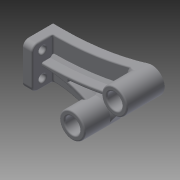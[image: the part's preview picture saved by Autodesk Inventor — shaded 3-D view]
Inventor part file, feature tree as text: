
AUTODESK INVENTOR PART (.ipt)
format: ipt  version: 2014 (Build 180170000, 170)  size: 399,360 bytes
history: native  units: in
note: dims shown in document units (in); Inventor stores cm internally (conversion verified against a paired STEP export)
features: extrude x6, sketch x6, fillet x2, chamfer x1
ambient origin geometry x8: Origin, YZ Plane, XZ Plane, XY Plane, X Axis, Y Axis, Z Axis, Center Point
bodies: Solid1 (feature_tree)
feature tree (15):
  extrude  "Extrusion1"  Depth=1.1713in
  extrude  "Extrusion2"  Depth=5.9055in
  extrude  "Extrusion3"  Depth=0.5315in
  extrude  "Extrusion4"  Depth=1.0441in
  extrude  "Extrusion5"  Depth=1.1024in
  chamfer  "Chamfer1"  Distance=0.8661in
  fillet  "Fillet1"  Radius=1.7717in
  fillet  "Fillet2"  Radius=0.1969in
  extrude  "Extrusion6"  Depth=0.0295in
  sketch  "Sketch1"  dims[d0=1.0441in d1=1.1713in]
  sketch  "Sketch3"  dims[d2=0.882in d3=5.9055in]
  sketch  "Sketch4"  dims[d5=0.315in d6=0.5315in]
  sketch  "Sketch6"  dims[d7=0.5906in d8=0.0in d9=1.0441in]
  sketch  "Sketch7"  dims[d10=0.882in d11=1.1024in]
  sketch  "Sketch8"  dims[d12=0.1969in d13=0.8661in d14=1.7717in d15=0.1969in d16=0.0in d17=0.4331in d18=0.1969in d19=0.0in d20=0.3543in d21=0.1378in d22=0.2362in d23=0.0in d24=0.0787in d25=0.8661in d26=0.4331in d29=0.0787in d30=0.0787in d31=0.2362in d32=0.0in d33=0.0551in d34=0.0787in d35=45.0deg d36=0.1181in d37=0.0295in d38=0.315in d39=0.0in]
